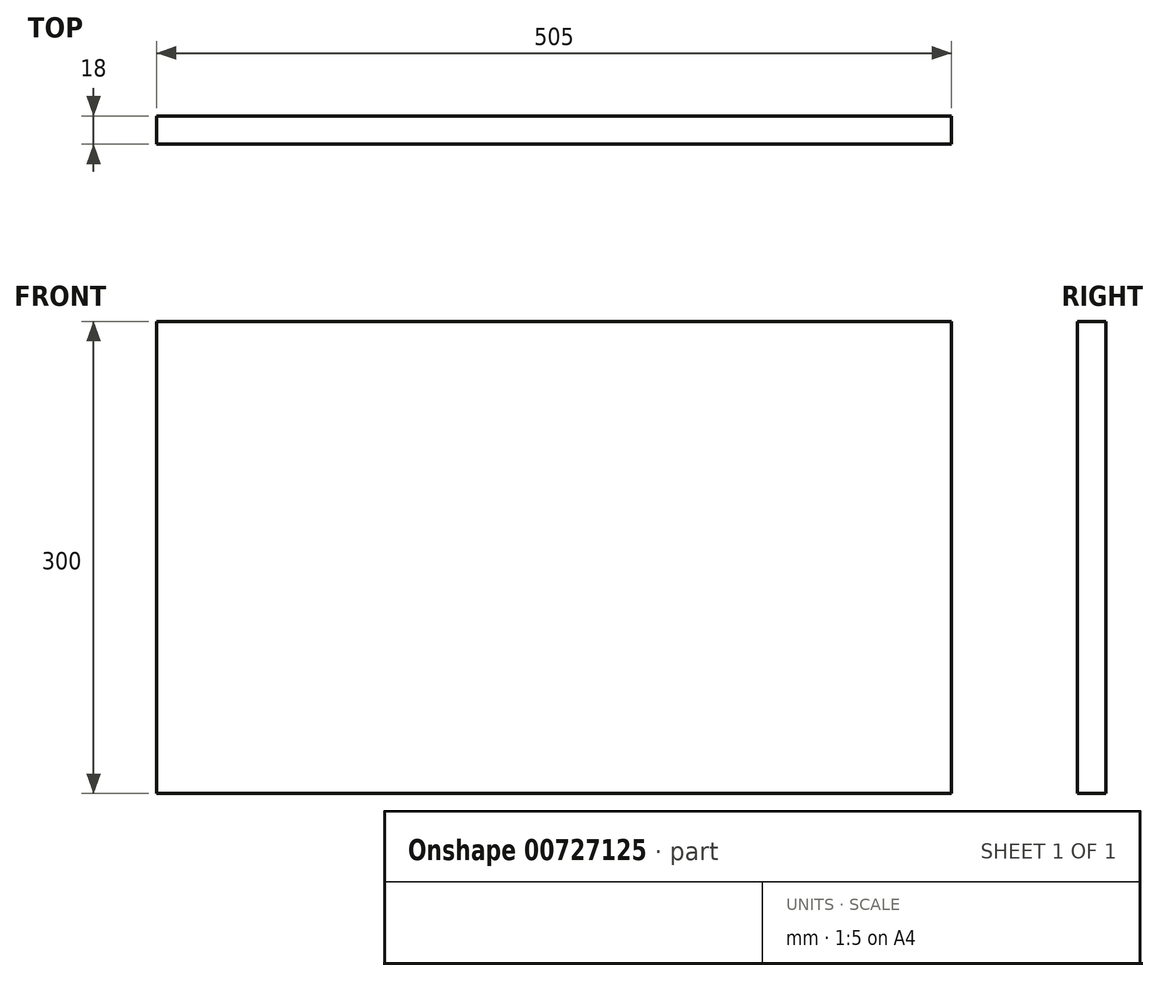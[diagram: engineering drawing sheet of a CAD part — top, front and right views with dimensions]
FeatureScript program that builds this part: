
annotation { "Feature Type Name" : "Feature", "Feature Type Description" : "" }
export const myFeature = defineFeature(function(context is Context, id is Id, definition is map)
    precondition{}
    {
        {
            var Q0;
            Q0=qCreatedBy(makeId("Front.planeOp"),FACE);
            var sketch = newSketch(context, id + "F0", { "sketchPlane" : qUnion([Q0])});
            skLineSegment(sketch, "E0.bottom", {"start": v(0, 0) * mm, "end": v(505, 0) * mm});
            skLineSegment(sketch, "E0.top", {"start": v(0, 300) * mm, "end": v(505, 300) * mm});
            skLineSegment(sketch, "E0.left", {"start": v(0, 0) * mm, "end": v(0, 300) * mm});
            skLineSegment(sketch, "E0.right", {"start": v(505, 0) * mm, "end": v(505, 300) * mm});
            skSolve(sketch);
        }
        {
            var Q0;
            Q0 = qSketchRegion(id + "F0", true);
            extrude(context, id + "F1", {"entities" : qUnion([Q0]), "depth" : 18 * mm, "offsetDistance" : 25 * mm});
        }
    });
